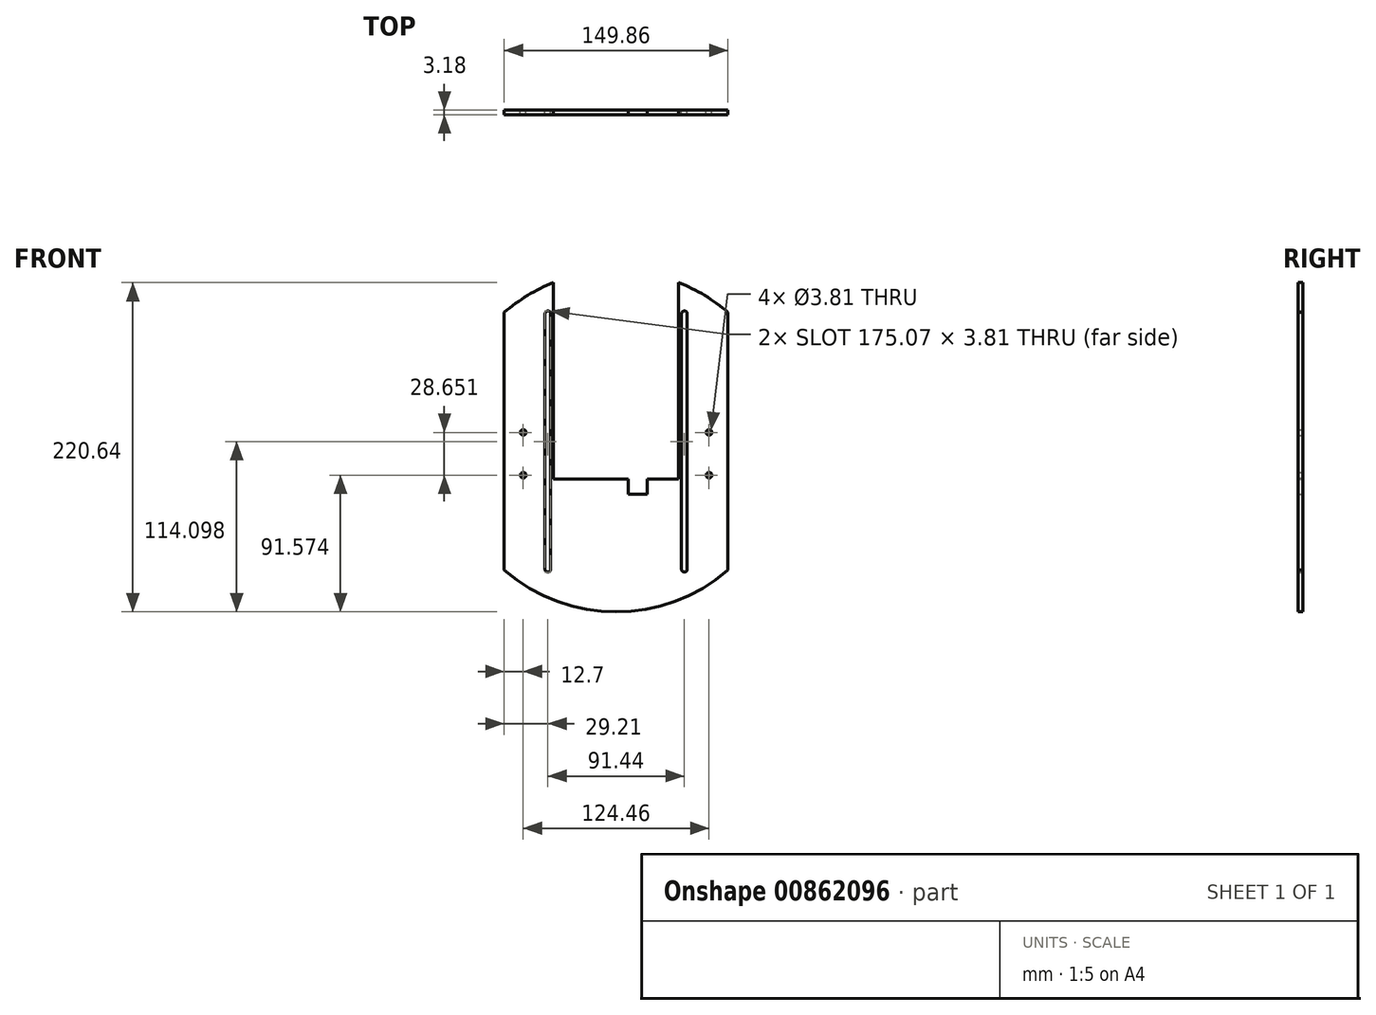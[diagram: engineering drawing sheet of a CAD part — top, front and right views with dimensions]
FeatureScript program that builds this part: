
annotation { "Feature Type Name" : "Feature", "Feature Type Description" : "" }
export const myFeature = defineFeature(function(context is Context, id is Id, definition is map)
    precondition{}
    {
        {
            var Q0;
            Q0=qCreatedBy(makeId("Front.planeOp"),FACE);
            var sketch = newSketch(context, id + "F0", { "sketchPlane" : qUnion([Q0])});
            skArc(sketch, "E0", {"start": v(-41.91, 106.34) * mm, "mid": v(-59.27, 97.73) * mm, "end": v(-74.93, 86.31) * mm});
            skLineSegment(sketch, "E1", {"start": v(-74.93, -86.31) * mm, "end": v(-74.93, 86.31) * mm});
            skArc(sketch, "E2.trimOffspring", {"start": v(-74.93, -86.31) * mm, "mid": v(-40, -107.07) * mm, "end": v(0, -114.3) * mm});
            skLineSegment(sketch, "E3", {"start": v(0, -95.25) * mm, "end": v(-25.4, -95.25) * mm, "construction": true});
            skLineSegment(sketch, "E4", {"start": v(-25.4, -95.25) * mm, "end": v(-25.4, -44.45) * mm, "construction": true});
            skLineSegment(sketch, "E5", {"start": v(-25.4, -44.45) * mm, "end": v(0, -44.45) * mm, "construction": true});
            skLineSegment(sketch, "E6", {"start": v(0, -25.4) * mm, "end": v(-41.91, -25.4) * mm, "construction": true});
            skLineSegment(sketch, "E7", {"start": v(-41.91, -25.4) * mm, "end": v(-41.91, 106.34) * mm, "construction": true});
            skLineSegment(sketch, "E8", {"start": v(0, -25.4) * mm, "end": v(-41.91, -25.4) * mm});
            skLineSegment(sketch, "E9", {"start": v(-41.91, -25.4) * mm, "end": v(-41.91, 106.34) * mm});
            skLineSegment(sketch, "E10", {"start": v(-74.93, -8.4) * mm, "end": v(-62.23, -8.4) * mm, "construction": true});
            skLineSegment(sketch, "E11", {"start": v(-62.23, -8.4) * mm, "end": v(-62.23, -22.73) * mm, "construction": true});
            skCircle(sketch, "E12", {"center": v(-62.23, -22.73) * mm, "radius": 1.9 * mm});
            skCircle(sketch, "E13.MirrorC", {"center": v(-62.23, 5.93) * mm, "radius": 1.9 * mm});
            skLineSegment(sketch, "E14", {"start": v(-62.23, -8.4) * mm, "end": v(-49.53, -8.4) * mm, "construction": true});
            skLineSegment(sketch, "E15", {"start": v(-49.53, -8.4) * mm, "end": v(-41.91, -8.4) * mm, "construction": true});
            skLineSegment(sketch, "E16", {"start": v(-45.72, 85.43) * mm, "end": v(-45.72, -85.83) * mm});
            skPoint(sketch, "E16.startSnap0", {"position": v(-45.72, -8.4) * mm});
            skArc(sketch, "E17.0.startCap", {"start": v(-47.62, 85.43) * mm, "mid": v(-45.72, 87.33) * mm, "end": v(-43.82, 85.43) * mm});
            skArc(sketch, "E17.0.endCap", {"start": v(-43.81, -85.83) * mm, "mid": v(-45.72, -87.74) * mm, "end": v(-47.62, -85.83) * mm});
            skLineSegment(sketch, "E17.0.left", {"start": v(-43.82, 85.43) * mm, "end": v(-43.81, -85.83) * mm});
            skLineSegment(sketch, "E17.0.right", {"start": v(-47.63, 85.43) * mm, "end": v(-47.62, -85.83) * mm});
            skCircle(sketch, "E18.MirrorC", {"center": v(62.23, -22.73) * mm, "radius": 1.9 * mm});
            skArc(sketch, "E19.MirrorCS", {"start": v(47.62, 85.43) * mm, "mid": v(45.72, 87.33) * mm, "end": v(43.82, 85.43) * mm});
            skArc(sketch, "E20.MirrorCS", {"start": v(43.81, -85.83) * mm, "mid": v(45.72, -87.74) * mm, "end": v(47.62, -85.83) * mm});
            skCircle(sketch, "E21.MirrorC", {"center": v(62.23, 5.93) * mm, "radius": 1.9 * mm});
            skLineSegment(sketch, "E22.MirrorCS", {"start": v(41.91, -25.4) * mm, "end": v(41.91, 106.34) * mm});
            skLineSegment(sketch, "E23.MirrorCS", {"start": v(0, -25.4) * mm, "end": v(8.26, -25.4) * mm});
            skLineSegment(sketch, "E24.MirrorCS", {"start": v(49.53, -8.4) * mm, "end": v(41.91, -8.4) * mm, "construction": true});
            skLineSegment(sketch, "E25.MirrorCS", {"start": v(62.23, -8.4) * mm, "end": v(62.23, -22.73) * mm, "construction": true});
            skLineSegment(sketch, "E26.MirrorCS", {"start": v(74.93, -8.4) * mm, "end": v(62.23, -8.4) * mm, "construction": true});
            skLineSegment(sketch, "E27.MirrorCS", {"start": v(62.23, -8.4) * mm, "end": v(49.53, -8.4) * mm, "construction": true});
            skLineSegment(sketch, "E28.MirrorCS", {"start": v(47.62, 85.43) * mm, "end": v(47.62, -85.83) * mm});
            skLineSegment(sketch, "E29.MirrorCS", {"start": v(43.81, 85.43) * mm, "end": v(43.81, -85.83) * mm});
            skLineSegment(sketch, "E30.MirrorCS", {"start": v(0, -25.4) * mm, "end": v(8.26, -25.4) * mm, "construction": true});
            skLineSegment(sketch, "E31.MirrorCS", {"start": v(25.4, -44.45) * mm, "end": v(0, -44.45) * mm, "construction": true});
            skPoint(sketch, "E32.MirrorP", {"position": v(45.72, -8.4) * mm});
            skArc(sketch, "E33.MirrorCS", {"start": v(41.91, 106.34) * mm, "mid": v(59.27, 97.73) * mm, "end": v(74.93, 86.31) * mm});
            skLineSegment(sketch, "E34.MirrorCS", {"start": v(25.4, -95.25) * mm, "end": v(25.4, -44.45) * mm, "construction": true});
            skLineSegment(sketch, "E35.MirrorCS", {"start": v(45.72, 85.43) * mm, "end": v(45.72, -85.83) * mm});
            skLineSegment(sketch, "E36.MirrorCS", {"start": v(41.91, -25.4) * mm, "end": v(41.91, 106.34) * mm, "construction": true});
            skLineSegment(sketch, "E37.MirrorCS", {"start": v(0, -95.25) * mm, "end": v(25.4, -95.25) * mm, "construction": true});
            skArc(sketch, "E38.MirrorCS", {"start": v(74.93, -86.31) * mm, "mid": v(40, -107.07) * mm, "end": v(0, -114.3) * mm});
            skLineSegment(sketch, "E39.MirrorCS", {"start": v(74.93, -86.31) * mm, "end": v(74.93, 86.31) * mm});
            skLineSegment(sketch, "E40", {"start": v(20.96, -25.4) * mm, "end": v(20.96, -35.56) * mm});
            skLineSegment(sketch, "E41", {"start": v(20.96, -35.56) * mm, "end": v(8.26, -35.56) * mm});
            skLineSegment(sketch, "E42", {"start": v(8.26, -35.56) * mm, "end": v(8.26, -25.4) * mm});
            skLineSegment(sketch, "E43.trimOffspring", {"start": v(20.96, -25.4) * mm, "end": v(41.91, -25.4) * mm, "construction": true});
            skLineSegment(sketch, "E44.trimOffspring", {"start": v(20.96, -25.4) * mm, "end": v(41.91, -25.4) * mm});
            skSolve(sketch);
        }
        {
            var Q0;
            Q0=makeQuery(id+"F0.imprint","IMPRINT",FACE,{"disambiguationData":[TD([[makeQuery(id+"F0.imprint","IMPRINT",EDGE,{"derivedFrom":sQuery(id+"F0.wireOp",EDGE,"E0")}),1.0]])]});
            extrude(context, id + "F1", {"entities" : qUnion([Q0]), "depth" : 3.17 * mm, "offsetDistance" : 25.4 * mm});
        }
    });
